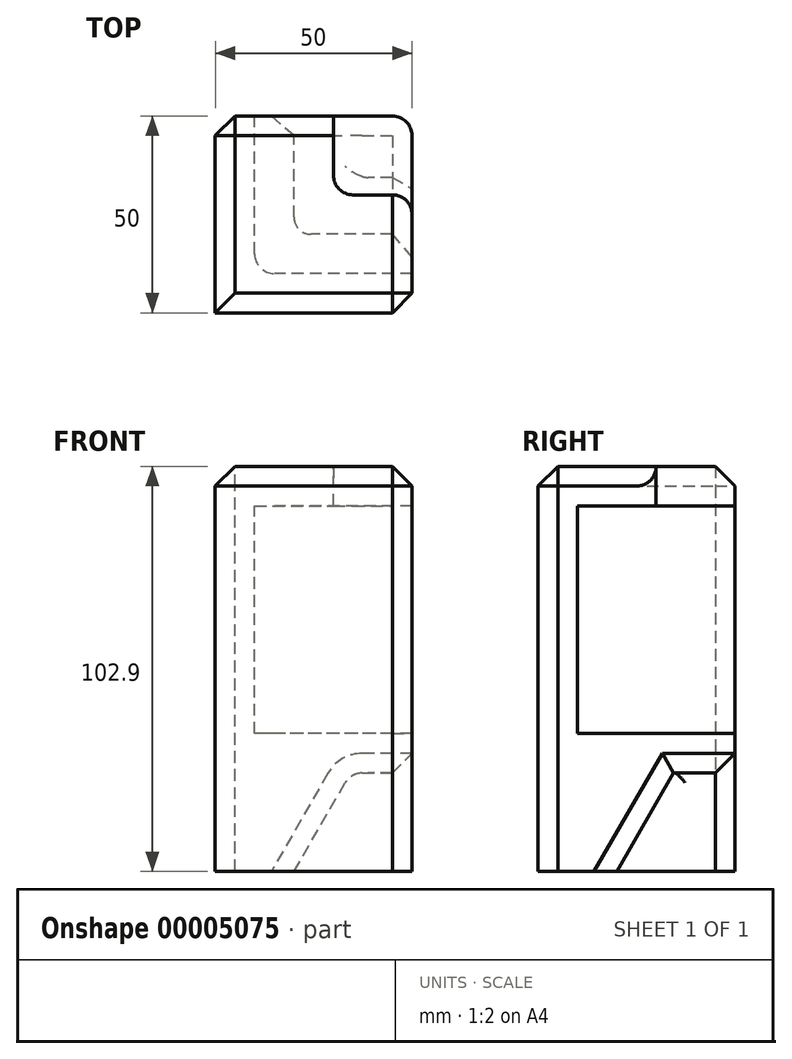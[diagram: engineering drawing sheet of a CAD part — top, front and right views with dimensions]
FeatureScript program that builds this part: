
annotation { "Feature Type Name" : "Feature", "Feature Type Description" : "" }
export const myFeature = defineFeature(function(context is Context, id is Id, definition is map)
    precondition{}
    {
        {
            var Q0;
            Q0=qCreatedBy(makeId("Front.planeOp"),FACE);
            var sketch = newSketch(context, id + "F0", { "sketchPlane" : qUnion([Q0])});
            skLineSegment(sketch, "E0", {"start": v(5.57, 28.78) * mm, "end": v(-34.43, 28.78) * mm});
            skLineSegment(sketch, "E1", {"start": v(-34.43, 28.78) * mm, "end": v(-34.43, -74.12) * mm});
            skLineSegment(sketch, "E2", {"start": v(-34.43, -74.12) * mm, "end": v(-14.43, -74.12) * mm});
            skLineSegment(sketch, "E3", {"start": v(-14.43, -74.12) * mm, "end": v(0, -49.12) * mm});
            skLineSegment(sketch, "E4", {"start": v(0, -49.12) * mm, "end": v(5.57, -49.12) * mm});
            skLineSegment(sketch, "E5", {"start": v(5.57, -49.12) * mm, "end": v(5.57, -39.12) * mm});
            skLineSegment(sketch, "E6", {"start": v(5.57, -39.12) * mm, "end": v(-24.43, -39.12) * mm});
            skLineSegment(sketch, "E7", {"start": v(-24.43, -39.12) * mm, "end": v(-24.43, 18.78) * mm});
            skLineSegment(sketch, "E8", {"start": v(-24.43, 18.78) * mm, "end": v(5.57, 18.78) * mm});
            skLineSegment(sketch, "E9", {"start": v(5.57, 18.78) * mm, "end": v(5.57, 28.78) * mm});
            skSolve(sketch);
        }
        {
            var Q0;
            Q0=makeQuery(id+"F0.imprint","IMPRINT",FACE,{"disambiguationData":[TD([[makeQuery(id+"F0.imprint","IMPRINT",EDGE,{"derivedFrom":sQuery(id+"F0.wireOp",EDGE,"E0")}),1.0]])]});
            extrude(context, id + "F1", {"entities" : qUnion([Q0]), "depth" : 50 * mm});
        }
        {
            var Q0;
            Q0=makeQuery(id+"F1.opExtrude","SWEPT_FACE",FACE,{"disambiguationData":[OSD([sQuery(id+"F0.wireOp",EDGE,"E1")])]});
            var sketch = newSketch(context, id + "F2", { "sketchPlane" : qUnion([Q0])});
            skLineSegment(sketch, "E10", {"start": v(0, 28.78) * mm, "end": v(50, 28.78) * mm});
            skLineSegment(sketch, "E11", {"start": v(50, 28.78) * mm, "end": v(50, -74.12) * mm});
            skLineSegment(sketch, "E12", {"start": v(50, -74.12) * mm, "end": v(30, -74.12) * mm});
            skLineSegment(sketch, "E13", {"start": v(30, -74.12) * mm, "end": v(15.57, -49.12) * mm});
            skLineSegment(sketch, "E14", {"start": v(0, -39.12) * mm, "end": v(40, -39.12) * mm});
            skLineSegment(sketch, "E15", {"start": v(40, -39.12) * mm, "end": v(40, 18.78) * mm});
            skLineSegment(sketch, "E16", {"start": v(40, 18.78) * mm, "end": v(0, 18.78) * mm});
            skLineSegment(sketch, "E17", {"start": v(0, 18.78) * mm, "end": v(0, 28.78) * mm});
            skLineSegment(sketch, "E18", {"start": v(15.57, -49.12) * mm, "end": v(0, -49.12) * mm});
            skLineSegment(sketch, "E19", {"start": v(0, -49.12) * mm, "end": v(0, -39.12) * mm});
            skSolve(sketch);
        }
        {
            var Q0;
            Q0 = qSketchRegion(id + "F2", true);
            var Q1;
            Q1=makeQuery(id+"F1.opExtrude","SWEPT_FACE",FACE,{"disambiguationData":[OSD([sQuery(id+"F0.wireOp",EDGE,"E5")])]});
            extrude(context, id + "F3", {"entities" : qUnion([Q0]), "operationType" : NewBodyOperationType.ADD, "oppositeDirection" : true, "endBoundEntity" : qUnion([Q1]), "depth" : 50 * mm});
        }
        {
            var Q0;
            Q0=makeQuery(id+"F3.boolean.opBoolean","MERGE",FACE,{"derivedFrom":[makeQuery(id+"F1.opExtrude","SWEPT_FACE",FACE,{"disambiguationData":[OSD([sQuery(id+"F0.wireOp",EDGE,"E0")])]}),makeQuery(id+"F3.opExtrude","SWEPT_FACE",FACE,{"disambiguationData":[OSD([sQuery(id+"F2.wireOp",EDGE,"E10")])]})]});
            var sketch = newSketch(context, id + "F4", { "sketchPlane" : qUnion([Q0])});
            skLineSegment(sketch, "E20.bottom", {"start": v(-4.43, 0) * mm, "end": v(25.93, 0) * mm});
            skLineSegment(sketch, "E20.top", {"start": v(-4.43, -20) * mm, "end": v(25.93, -20) * mm});
            skLineSegment(sketch, "E20.left", {"start": v(-4.43, 0) * mm, "end": v(-4.43, -20) * mm});
            skLineSegment(sketch, "E20.right", {"start": v(25.93, 0) * mm, "end": v(25.93, -20) * mm});
            skSolve(sketch);
        }
        {
            var Q0;
            {var subQ5=sQuery(id+"F4.wireOp",EDGE,"E20.right");Q0=makeQuery(id+"F4.imprint","IMPRINT",FACE,{"disambiguationData":[TD([[makeQuery(id+"F4.imprint","IMPRINT",EDGE,{"derivedFrom":subQ5}),-1.0]])]});}
            var Q1;
            {var subQ7=sQuery(id+"F4.wireOp",EDGE,"E20.left");Q1=makeQuery(id+"F4.imprint","IMPRINT",FACE,{"disambiguationData":[TD([[makeQuery(id+"F4.imprint","IMPRINT",EDGE,{"derivedFrom":subQ7}),1.0]])]});}
            var Q2;
            Q2=makeQuery(id+"F3.boolean.opBoolean","MERGE",FACE,{"derivedFrom":[makeQuery(id+"F1.opExtrude","SWEPT_FACE",FACE,{"disambiguationData":[OSD([sQuery(id+"F0.wireOp",EDGE,"E8")])]}),makeQuery(id+"F3.opExtrude","SWEPT_FACE",FACE,{"disambiguationData":[OSD([sQuery(id+"F2.wireOp",EDGE,"E16")])]})]});
            extrude(context, id + "F5", {"entities" : qUnion([Q0, Q1]), "operationType" : NewBodyOperationType.REMOVE, "oppositeDirection" : true, "endBoundEntity" : qUnion([Q2]), "depth" : 20.55 * mm});
        }
        {
            var Q0;
            Q0=makeQuery(id+"F1.opExtrude","SWEPT_EDGE",EDGE,{"disambiguationData":[OSD([sQuery(id+"F0.wireOp",EDGE,"E0"),sQuery(id+"F0.wireOp",EDGE,"E1")])]});
            var Q1;
            Q1=makeQuery(id+"F3.opExtrude","CAP_EDGE",EDGE,{"disambiguationData":[OSD([sQuery(id+"F2.wireOp",EDGE,"E11")])],"isStart":false});
            var Q2;
            Q2=makeQuery(id+"F1.opExtrude","CAP_EDGE",EDGE,{"disambiguationData":[OSD([sQuery(id+"F0.wireOp",EDGE,"E1")])],"isStart":true});
            var Q3;
            Q3=makeQuery(id+"F3.boolean.opBoolean","MERGE",EDGE,{"derivedFrom":[makeQuery(id+"F1.opExtrude","CAP_EDGE",EDGE,{"disambiguationData":[OSD([sQuery(id+"F0.wireOp",EDGE,"E0")])],"isStart":false}),makeQuery(id+"F3.opExtrude","SWEPT_EDGE",EDGE,{"disambiguationData":[OSD([sQuery(id+"F2.wireOp",EDGE,"E10"),sQuery(id+"F2.wireOp",EDGE,"E11")])]})]});
            var Q4;
            Q4=makeQuery(id+"F3.opExtrude","CAP_EDGE",EDGE,{"disambiguationData":[OSD([sQuery(id+"F2.wireOp",EDGE,"E10")])],"isStart":false});
            var Q5;
            Q5=makeQuery(id+"F5.boolean.opBoolean","COPY",EDGE,{"derivedFrom":makeQuery(id+"F5.opExtrude","CAP_EDGE",EDGE,{"disambiguationData":[OSD([sQuery(id+"F4.wireOp",EDGE,"E20.top")])],"isStart":true})});
            var Q6;
            Q6=makeQuery(id+"F3.boolean.opBoolean","MERGE",EDGE,{"derivedFrom":[makeQuery(id+"F1.opExtrude","CAP_EDGE",EDGE,{"disambiguationData":[OSD([sQuery(id+"F0.wireOp",EDGE,"E0")])],"isStart":true}),makeQuery(id+"F3.opExtrude","SWEPT_EDGE",EDGE,{"disambiguationData":[OSD([sQuery(id+"F2.wireOp",EDGE,"E10"),sQuery(id+"F2.wireOp",EDGE,"E17")])]})]});
            var Q7;
            Q7=makeQuery(id+"F5.boolean.opBoolean","COPY",EDGE,{"derivedFrom":makeQuery(id+"F5.opExtrude","CAP_EDGE",EDGE,{"disambiguationData":[OSD([sQuery(id+"F4.wireOp",EDGE,"E20.left")])],"isStart":true})});
            chamfer(context, id + "F6", {"entities" : qUnion([Q0, Q1, Q2, Q3, Q4, Q5, Q6, Q7]), "width" : 5 * mm, "tangentPropagation" : true});
        }
        {
            var Q0;
            Q0=makeQuery(id+"F3.opExtrude","SWEPT_EDGE",EDGE,{"disambiguationData":[OSD([sQuery(id+"F2.wireOp",EDGE,"E13"),sQuery(id+"F2.wireOp",EDGE,"E18")])]});
            var Q1;
            Q1=makeQuery(id+"F1.opExtrude","SWEPT_EDGE",EDGE,{"disambiguationData":[OSD([sQuery(id+"F0.wireOp",EDGE,"E3"),sQuery(id+"F0.wireOp",EDGE,"E4")])]});
            var Q2;
            Q2=makeQuery(id+"F3.boolean.opBoolean","INTERSECT",EDGE,{"derivedFrom":[makeQuery(id+"F1.opExtrude","SWEPT_FACE",FACE,{"disambiguationData":[OSD([sQuery(id+"F0.wireOp",EDGE,"E3")])]}),makeQuery(id+"F3.opExtrude","SWEPT_FACE",FACE,{"disambiguationData":[OSD([sQuery(id+"F2.wireOp",EDGE,"E13")])]})]});
            var Q3;
            Q3=makeQuery(id+"F5.boolean.opBoolean","INTERSECT",EDGE,{"derivedFrom":[makeQuery(id+"F3.opExtrude","CAP_FACE",FACE,{"disambiguationData":[OSD([sQuery(id+"F2.wireOp",EDGE,"E10"),sQuery(id+"F2.wireOp",EDGE,"E11"),sQuery(id+"F2.wireOp",EDGE,"E12"),sQuery(id+"F2.wireOp",EDGE,"E13"),sQuery(id+"F2.wireOp",EDGE,"E14"),sQuery(id+"F2.wireOp",EDGE,"E15"),sQuery(id+"F2.wireOp",EDGE,"E16"),sQuery(id+"F2.wireOp",EDGE,"E17"),sQuery(id+"F2.wireOp",EDGE,"E18"),sQuery(id+"F2.wireOp",EDGE,"E19")])],"isStart":false}),makeQuery(id+"F5.opExtrude","SWEPT_FACE",FACE,{"disambiguationData":[OSD([sQuery(id+"F4.wireOp",EDGE,"E20.top")])]})]});
            var Q4;
            Q4=makeQuery(id+"F5.boolean.opBoolean","COPY",EDGE,{"derivedFrom":makeQuery(id+"F5.opExtrude","SWEPT_EDGE",EDGE,{"disambiguationData":[OSD([sQuery(id+"F0.wireOp",EDGE,"E0"),sQuery(id+"F2.wireOp",EDGE,"E10"),sQuery(id+"F2.wireOp",EDGE,"E17"),sQuery(id+"F4.wireOp",EDGE,"E20.bottom"),sQuery(id+"F4.wireOp",EDGE,"E20.left")])]})});
            var Q5;
            Q5=makeQuery(id+"F6.opChamfer","BLEND_EDGE",EDGE,{"blendedFrom":[makeQuery(id+"F5.boolean.opBoolean","COPY",EDGE,{"derivedFrom":makeQuery(id+"F5.opExtrude","CAP_EDGE",EDGE,{"disambiguationData":[OSD([sQuery(id+"F4.wireOp",EDGE,"E20.left")])],"isStart":true})}),makeQuery(id+"F3.boolean.opBoolean","MERGE",EDGE,{"derivedFrom":[makeQuery(id+"F1.opExtrude","CAP_EDGE",EDGE,{"disambiguationData":[OSD([sQuery(id+"F0.wireOp",EDGE,"E0")])],"isStart":true}),makeQuery(id+"F3.opExtrude","SWEPT_EDGE",EDGE,{"disambiguationData":[OSD([sQuery(id+"F2.wireOp",EDGE,"E10"),sQuery(id+"F2.wireOp",EDGE,"E17")])]})]})],"blendedInto":[]});
            var Q6;
            Q6=makeQuery(id+"F6.opChamfer","BLEND_EDGE",EDGE,{"blendedFrom":[makeQuery(id+"F5.boolean.opBoolean","COPY",EDGE,{"derivedFrom":makeQuery(id+"F5.opExtrude","CAP_EDGE",EDGE,{"disambiguationData":[OSD([sQuery(id+"F4.wireOp",EDGE,"E20.top")])],"isStart":true})}),makeQuery(id+"F3.opExtrude","CAP_EDGE",EDGE,{"disambiguationData":[OSD([sQuery(id+"F2.wireOp",EDGE,"E10")])],"isStart":false})],"blendedInto":[]});
            var Q7;
            Q7=makeQuery(id+"F5.boolean.opBoolean","COPY",EDGE,{"derivedFrom":makeQuery(id+"F5.opExtrude","SWEPT_EDGE",EDGE,{"disambiguationData":[OSD([sQuery(id+"F4.wireOp",EDGE,"E20.top"),sQuery(id+"F4.wireOp",EDGE,"E20.left")])]})});
            var Q8;
            Q8=makeQuery(id+"F6.opChamfer","BLEND_EDGE",EDGE,{"blendedFrom":[makeQuery(id+"F5.boolean.opBoolean","COPY",EDGE,{"derivedFrom":makeQuery(id+"F5.opExtrude","CAP_EDGE",EDGE,{"disambiguationData":[OSD([sQuery(id+"F4.wireOp",EDGE,"E20.top")])],"isStart":true})}),makeQuery(id+"F5.boolean.opBoolean","COPY",EDGE,{"derivedFrom":makeQuery(id+"F5.opExtrude","CAP_EDGE",EDGE,{"disambiguationData":[OSD([sQuery(id+"F4.wireOp",EDGE,"E20.left")])],"isStart":true})})],"blendedInto":[]});
            var Q9;
            Q9=makeQuery(id+"F3.opExtrude","CAP_EDGE",EDGE,{"disambiguationData":[OSD([sQuery(id+"F2.wireOp",EDGE,"E19")])],"isStart":false});
            fillet(context, id + "F7", {"entities" : qUnion([Q0, Q1, Q2, Q3, Q4, Q5, Q6, Q7, Q8, Q9]), "radius" : 5 * mm, "tangentPropagation" : true, "allowEdgeOverflow" : false});
        }
        {
            var Q0;
            Q0=makeQuery(id+"F3.opExtrude","CAP_EDGE",EDGE,{"disambiguationData":[OSD([sQuery(id+"F2.wireOp",EDGE,"E13")])],"isStart":false});
            var Q1;
            Q1=makeQuery(id+"F3.boolean.opBoolean","MERGE",EDGE,{"derivedFrom":[makeQuery(id+"F1.opExtrude","CAP_EDGE",EDGE,{"disambiguationData":[OSD([sQuery(id+"F0.wireOp",EDGE,"E4")])],"isStart":true}),makeQuery(id+"F3.opExtrude","SWEPT_EDGE",EDGE,{"disambiguationData":[OSD([sQuery(id+"F0.wireOp",EDGE,"E1"),sQuery(id+"F2.wireOp",EDGE,"E18"),sQuery(id+"F2.wireOp",EDGE,"E19")])]})]});
            var Q2;
            Q2=makeQuery(id+"F3.opExtrude","CAP_EDGE",EDGE,{"disambiguationData":[OSD([sQuery(id+"F2.wireOp",EDGE,"E19")])],"isStart":false});
            chamfer(context, id + "F8", {"entities" : qUnion([Q0, Q1, Q2]), "width" : 5 * mm, "tangentPropagation" : true});
        }
        {
            var Q0;
            Q0=makeQuery(id+"F3.boolean.opBoolean","INTERSECT",EDGE,{"derivedFrom":[makeQuery(id+"F1.opExtrude","SWEPT_FACE",FACE,{"disambiguationData":[OSD([sQuery(id+"F0.wireOp",EDGE,"E7")])]}),makeQuery(id+"F3.opExtrude","SWEPT_FACE",FACE,{"disambiguationData":[OSD([sQuery(id+"F2.wireOp",EDGE,"E15")])]})]});
            fillet(context, id + "F9", {"entities" : qUnion([Q0]), "radius" : 5 * mm, "tangentPropagation" : true, "allowEdgeOverflow" : false});
        }
    });
